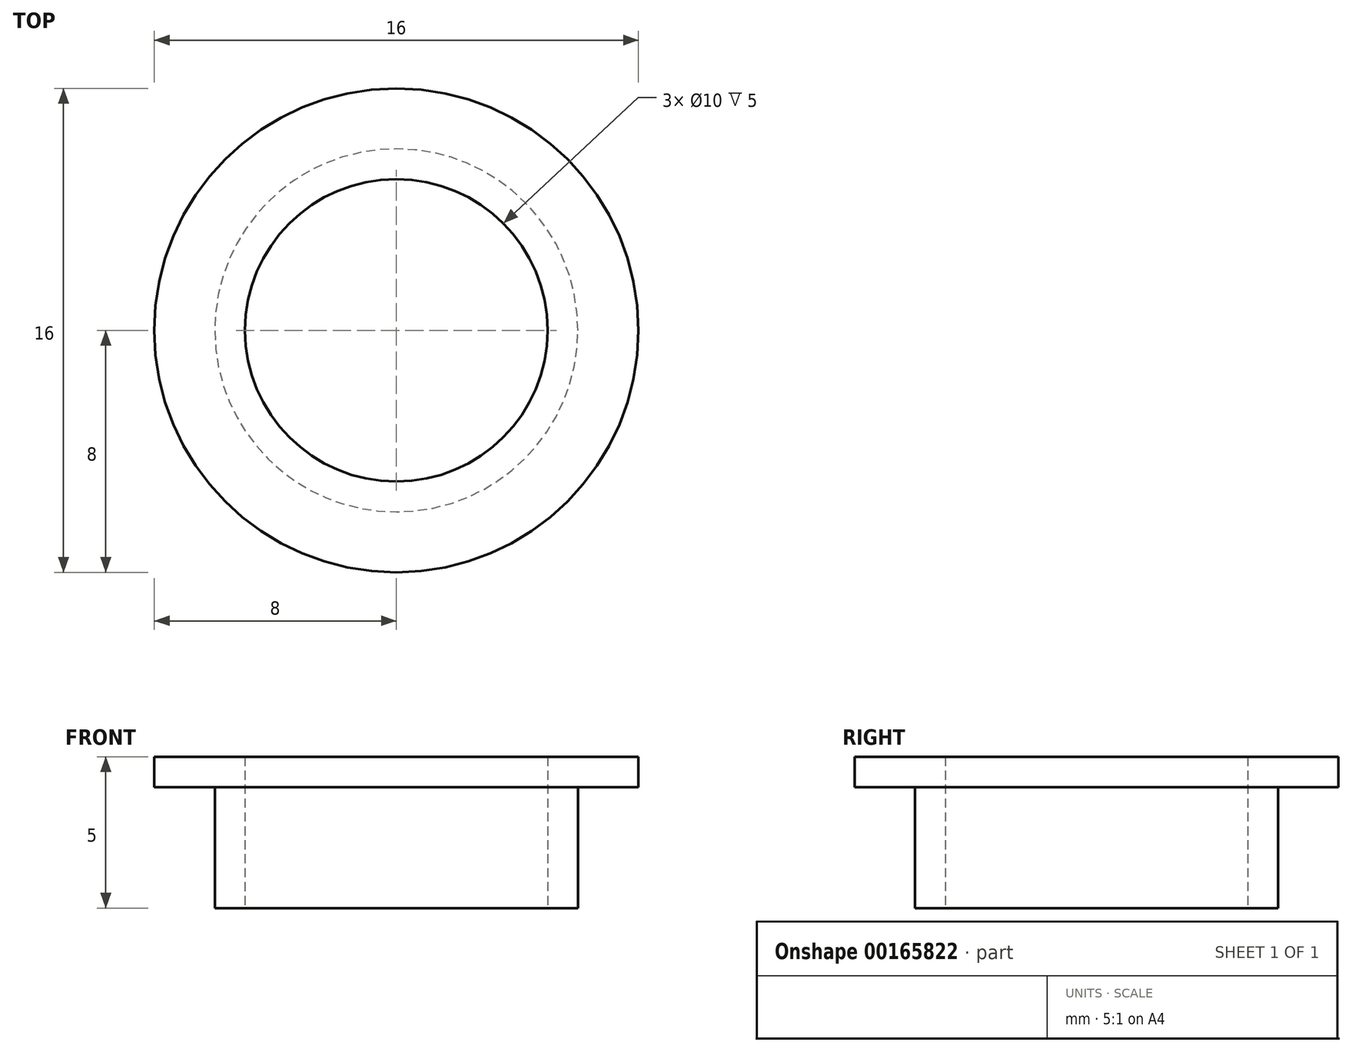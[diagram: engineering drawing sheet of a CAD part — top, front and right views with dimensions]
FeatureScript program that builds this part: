
annotation { "Feature Type Name" : "Feature", "Feature Type Description" : "" }
export const myFeature = defineFeature(function(context is Context, id is Id, definition is map)
    precondition{}
    {
        {
            var Q0;
            Q0=qCreatedBy(makeId("Front.planeOp"),FACE);
            var sketch = newSketch(context, id + "F0", { "sketchPlane" : qUnion([Q0])});
            skLineSegment(sketch, "E0", {"start": v(-5, 0) * mm, "end": v(-5, 5) * mm});
            skLineSegment(sketch, "E1", {"start": v(-5, 5) * mm, "end": v(-8, 5) * mm});
            skLineSegment(sketch, "E2", {"start": v(-8, 5) * mm, "end": v(-8, 4) * mm});
            skLineSegment(sketch, "E3", {"start": v(-8, 4) * mm, "end": v(-6, 4) * mm});
            skLineSegment(sketch, "E4", {"start": v(-6, 4) * mm, "end": v(-6, 0) * mm});
            skLineSegment(sketch, "E5", {"start": v(-6, 0) * mm, "end": v(-5, 0) * mm});
            skLineSegment(sketch, "E6", {"start": v(0, 0) * mm, "end": v(0, 10) * mm, "construction": true});
            skSolve(sketch);
        }
        {
            var Q0;
            Q0=makeQuery(id+"F0.imprint","IMPRINT",FACE,{"disambiguationData":[TD([[makeQuery(id+"F0.imprint","IMPRINT",EDGE,{"derivedFrom":sQuery(id+"F0.wireOp",EDGE,"E0")}),1.0]])]});
            var Q1;
            Q1=sQuery(id+"F0.wireOp",EDGE,"E6");
            revolve(context, id + "F1", {"entities" : qUnion([Q0]), "axis" : qUnion([Q1]), "revolveType" : RevolveType.FULL});
        }
    });
